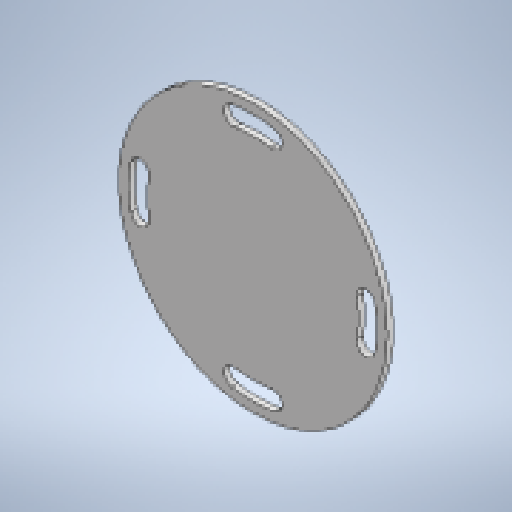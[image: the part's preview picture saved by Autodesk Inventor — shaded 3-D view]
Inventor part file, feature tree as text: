
AUTODESK INVENTOR PART (.ipt)
format: ipt  version: 2025 (Build 290162010, 162A)  size: 166,912 bytes
history: native  units: mm
features: sketch x2, sheet_metal_op x1, extrude x1, pattern_circular x1, other x1
ambient origin geometry x8: Origin, YZ Plane, XZ Plane, XY Plane, X Axis, Y Axis, Z Axis, Center Point
bodies: Solid1 (feature_tree)
feature tree (6):
  sheet_metal_op  "Face1"
  extrude  "Extrusion1"  Depth=4.0mm
  pattern_circular  "Circular Pattern1"  Count=4 Angle=360.0deg
  sketch  "Sketch1"  dims[d0=175.0mm d1=4.0mm]
  other  "Plate1"
  sketch  "Sketch2"  dims[d11=0.0mm d12=0.0mm d13=40.0mm d14=360.0deg d19=12.0mm d20=3.490659mm d21=75.0mm]
